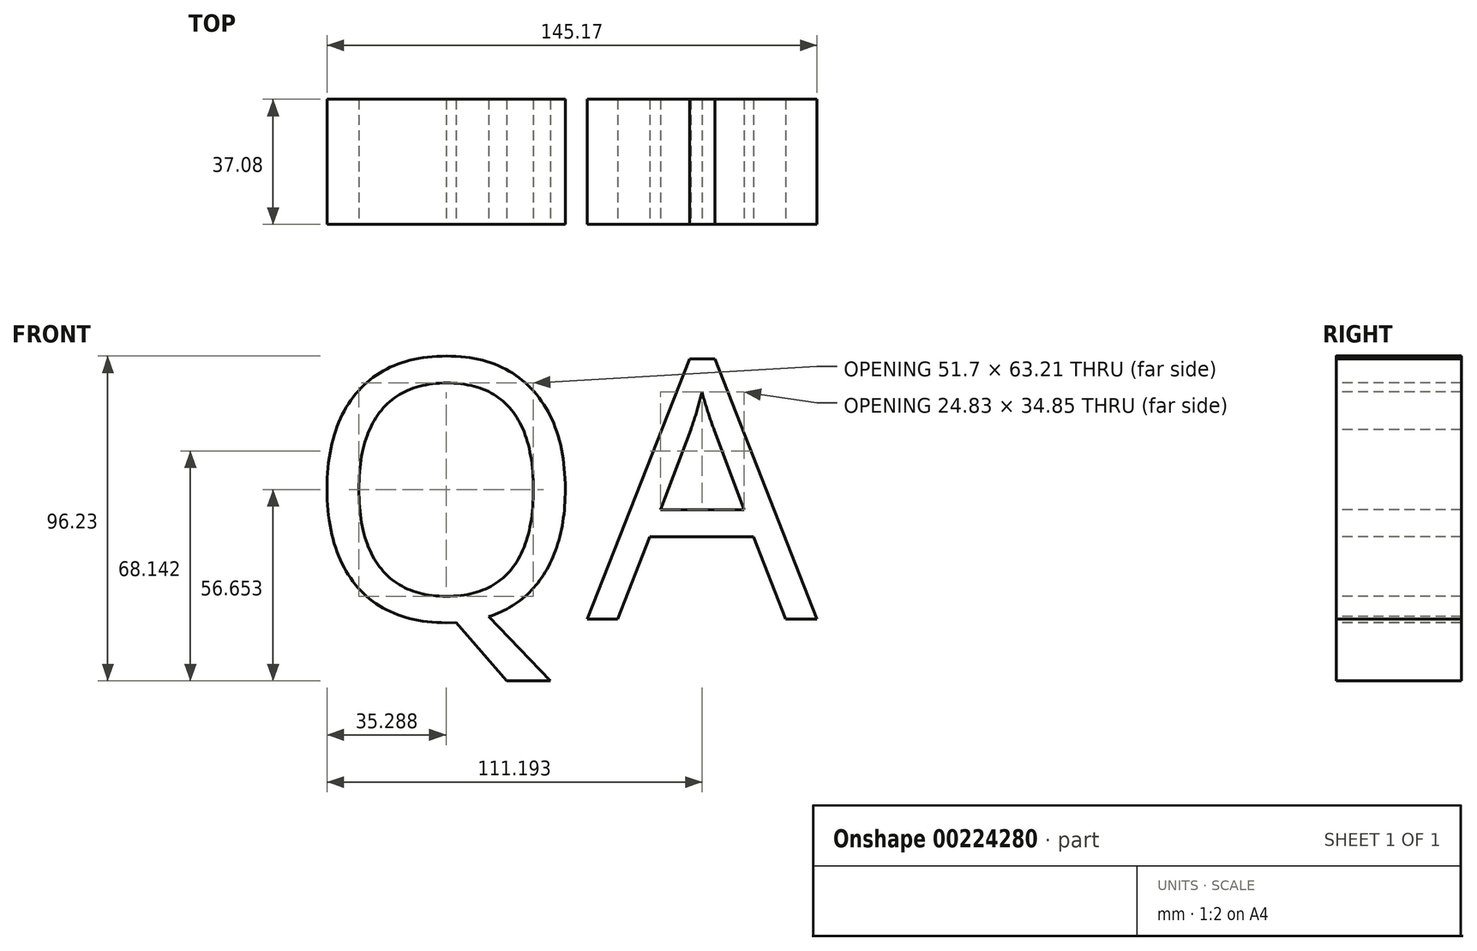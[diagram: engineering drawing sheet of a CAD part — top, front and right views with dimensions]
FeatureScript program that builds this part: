
annotation { "Feature Type Name" : "Feature", "Feature Type Description" : "" }
export const myFeature = defineFeature(function(context is Context, id is Id, definition is map)
    precondition{}
    {
        {
            var Q0;
            Q0=qCreatedBy(makeId("Front.planeOp"),FACE);
            var sketch = newSketch(context, id + "F0", { "sketchPlane" : qUnion([Q0])});
            skText(sketch, "E0", { "text": "QA", "fontName": "OpenSans-Regular.ttf"});
            const initialGuessF0  = {"E0": [-0.06068, -0.0344, 1, 0, 0.0774]};
            skSetInitialGuess(sketch, initialGuessF0);
            skSolve(sketch);
        }
        {
            var Q0;
            Q0 = qSketchRegion(id + "F0", true);
            extrude(context, id + "F1", {"entities" : qUnion([Q0]), "oppositeDirection" : true, "depth" : 37.08 * mm});
        }
    });
